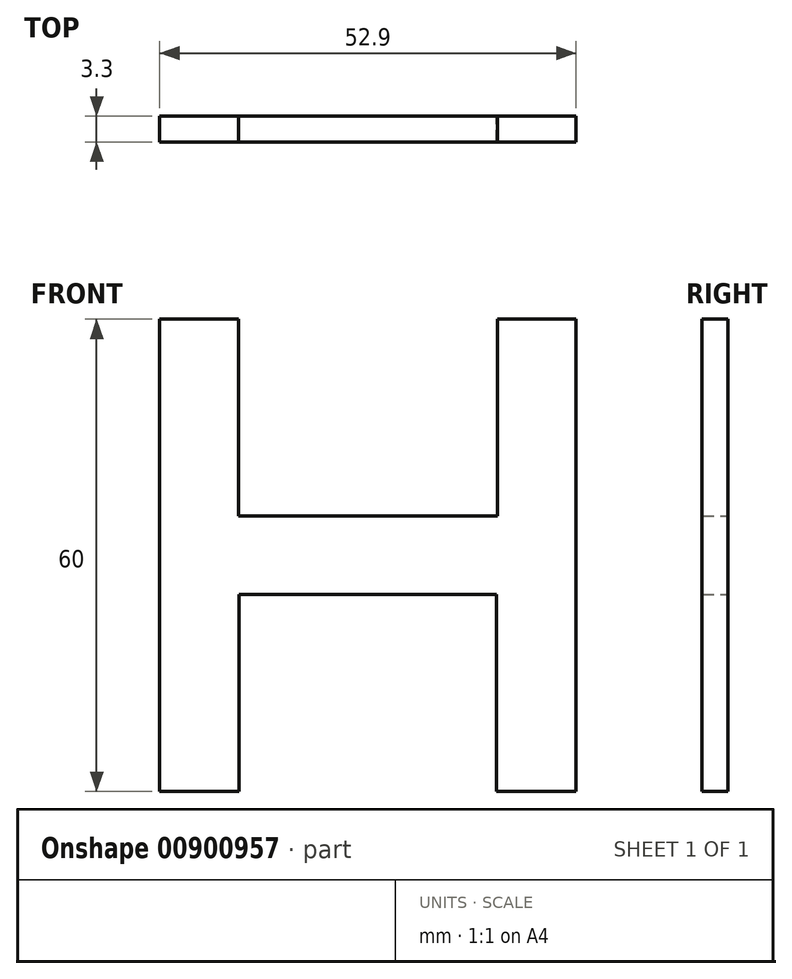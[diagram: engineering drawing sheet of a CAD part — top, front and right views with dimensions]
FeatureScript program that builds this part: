
annotation { "Feature Type Name" : "Feature", "Feature Type Description" : "" }
export const myFeature = defineFeature(function(context is Context, id is Id, definition is map)
    precondition{}
    {
        {
            var Q0;
            Q0=qCreatedBy(makeId("Front.planeOp"),FACE);
            var sketch = newSketch(context, id + "F0", { "sketchPlane" : qUnion([Q0])});
            skLineSegment(sketch, "E0", {"start": v(0, 0.94) * mm, "end": v(16.45, 0.94) * mm});
            skLineSegment(sketch, "E1", {"start": v(16.45, 0.94) * mm, "end": v(16.45, 25.94) * mm});
            skLineSegment(sketch, "E2", {"start": v(16.45, 25.94) * mm, "end": v(26.45, 25.94) * mm});
            skLineSegment(sketch, "E3", {"start": v(26.45, 25.94) * mm, "end": v(26.45, -34.06) * mm});
            skLineSegment(sketch, "E4", {"start": v(26.45, -34.06) * mm, "end": v(16.35, -34.06) * mm});
            skLineSegment(sketch, "E5", {"start": v(16.35, -34.06) * mm, "end": v(16.35, -9.06) * mm});
            skLineSegment(sketch, "E6", {"start": v(16.35, -9.06) * mm, "end": v(0, -9.06) * mm});
            skLineSegment(sketch, "E7.MirrorCS", {"start": v(-16.45, 25.94) * mm, "end": v(-26.45, 25.94) * mm});
            skLineSegment(sketch, "E8.MirrorCS", {"start": v(-26.45, 25.94) * mm, "end": v(-26.45, -34.06) * mm});
            skLineSegment(sketch, "E9.MirrorCS", {"start": v(-16.35, -34.06) * mm, "end": v(-16.35, -9.06) * mm});
            skLineSegment(sketch, "E10.MirrorCS", {"start": v(-26.45, -34.06) * mm, "end": v(-16.35, -34.06) * mm});
            skLineSegment(sketch, "E11.MirrorCS", {"start": v(-16.45, 0.94) * mm, "end": v(-16.45, 25.94) * mm});
            skLineSegment(sketch, "E12.MirrorCS", {"start": v(0, 0.94) * mm, "end": v(-16.45, 0.94) * mm});
            skLineSegment(sketch, "E13.MirrorCS", {"start": v(-16.35, -9.06) * mm, "end": v(0, -9.06) * mm});
            skSolve(sketch);
        }
        {
            var Q0;
            Q0=makeQuery(id+"F0.imprint","IMPRINT",FACE,{"disambiguationData":[TD([[makeQuery(id+"F0.imprint","IMPRINT",EDGE,{"derivedFrom":sQuery(id+"F0.wireOp",EDGE,"E0")}),-1.0]])]});
            extrude(context, id + "F1", {"entities" : qUnion([Q0]), "depth" : 3.3 * mm, "offsetDistance" : 25 * mm});
        }
    });
